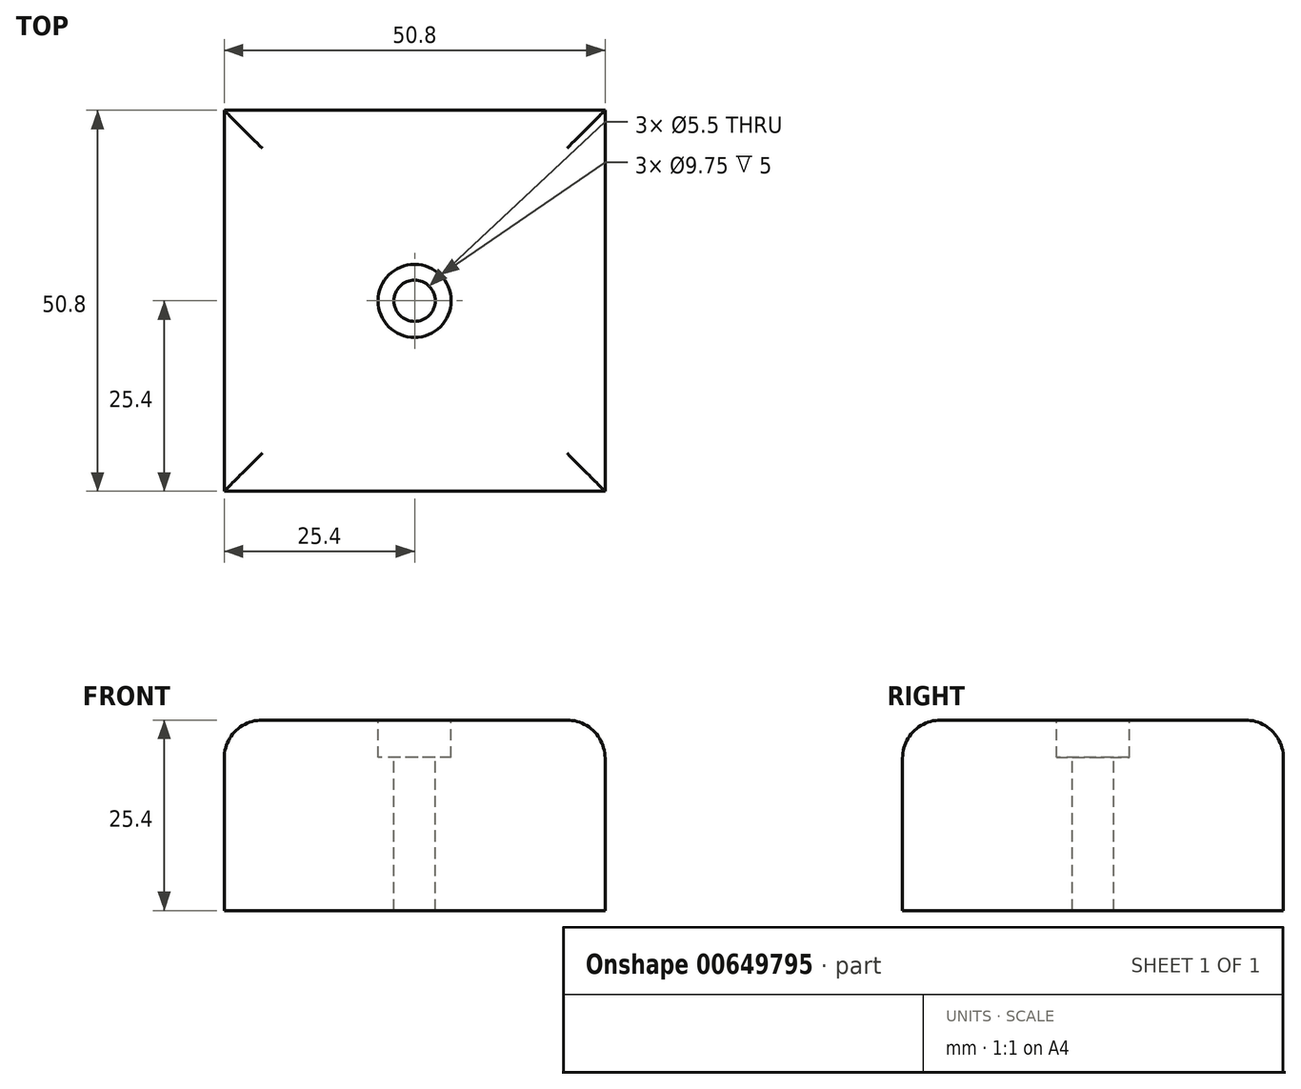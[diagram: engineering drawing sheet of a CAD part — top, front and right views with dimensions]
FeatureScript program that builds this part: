
annotation { "Feature Type Name" : "Feature", "Feature Type Description" : "" }
export const myFeature = defineFeature(function(context is Context, id is Id, definition is map)
    precondition{}
    {
        {
            var Q0;
            Q0=qCreatedBy(makeId("Top.planeOp"),FACE);
            var sketch = newSketch(context, id + "F0", { "sketchPlane" : qUnion([Q0])});
            skLineSegment(sketch, "E0.bottom", {"start": v(25.4, 25.4) * mm, "end": v(-25.4, 25.4) * mm});
            skLineSegment(sketch, "E0.top", {"start": v(25.4, -25.4) * mm, "end": v(-25.4, -25.4) * mm});
            skLineSegment(sketch, "E0.left", {"start": v(25.4, 25.4) * mm, "end": v(25.4, -25.4) * mm});
            skLineSegment(sketch, "E0.right", {"start": v(-25.4, 25.4) * mm, "end": v(-25.4, -25.4) * mm});
            skPoint(sketch, "E0.middle", {"position": v(0, 0) * mm});
            skSolve(sketch);
        }
        {
            var Q0;
            Q0 = qSketchRegion(id + "F0", true);
            extrude(context, id + "F1", {"entities" : qUnion([Q0]), "depth" : 25.4 * mm, "offsetDistance" : 25.4 * mm});
        }
        {
            var Q0;
            Q0=makeQuery(id+"F1.opExtrude","CAP_FACE",FACE,{"disambiguationData":[OSD([sQuery(id+"F0.wireOp",EDGE,"E0.bottom"),sQuery(id+"F0.wireOp",EDGE,"E0.top"),sQuery(id+"F0.wireOp",EDGE,"E0.left"),sQuery(id+"F0.wireOp",EDGE,"E0.right")])],"isStart":false});
            var sketch = newSketch(context, id + "F2", { "sketchPlane" : qUnion([Q0])});
            skPoint(sketch, "E1", {"position": v(0, 0) * mm});
            skSolve(sketch);
        }
        {
            var Q0;
            Q0=sQuery(id+"F2.wireOp",VERTEX,"E1");
            var Q1;
            Q1=makeQuery(id+"F1.opExtrude","SWEPT_BODY",BODY,{"disambiguationData":[OSD([sQuery(id+"F0.wireOp",EDGE,"E0.bottom"),sQuery(id+"F0.wireOp",EDGE,"E0.top"),sQuery(id+"F0.wireOp",EDGE,"E0.left"),sQuery(id+"F0.wireOp",EDGE,"E0.right")])]});
            hole(context, id + "F3", {"style" : HoleStyle.C_BORE, "endStyle" : HoleEndStyle.THROUGH, "standardTappedOrClearance" : lookupTablePath({ "standard" : "ISO", "fit" : "Normal", "size" : "M5", "type" : "Clearance" }), "standardBlindInLast" : lookupTablePath({ "fit" : "Standard", "standard" : "ISO", "size" : "M5", "type" : "Clearance" }), "holeDiameter" : 5.5 * mm, "cBoreDiameter" : 9.75 * mm, "cBoreDepth" : 5 * mm, "majorDiameter" : 6.35 * mm, "isTappedThrough" : true, "tappedDepth" : 12.7 * mm, "tapClearance" : 3, "locations" : qUnion([Q0]), "scope" : qUnion([Q1])});
        }
        {
            var Q0;
            Q0=makeQuery(id+"F1.opExtrude","CAP_EDGE",EDGE,{"disambiguationData":[OSD([sQuery(id+"F0.wireOp",EDGE,"E0.right")])],"isStart":false});
            var Q1;
            Q1=makeQuery(id+"F1.opExtrude","CAP_EDGE",EDGE,{"disambiguationData":[OSD([sQuery(id+"F0.wireOp",EDGE,"E0.bottom")])],"isStart":false});
            var Q2;
            Q2=makeQuery(id+"F1.opExtrude","CAP_EDGE",EDGE,{"disambiguationData":[OSD([sQuery(id+"F0.wireOp",EDGE,"E0.left")])],"isStart":false});
            var Q3;
            Q3=makeQuery(id+"F1.opExtrude","CAP_EDGE",EDGE,{"disambiguationData":[OSD([sQuery(id+"F0.wireOp",EDGE,"E0.top")])],"isStart":false});
            fillet(context, id + "F4", {"entities" : qUnion([Q0, Q1, Q2, Q3]), "radius" : 5.08 * mm, "tangentPropagation" : true, "allowEdgeOverflow" : false});
        }
    });
